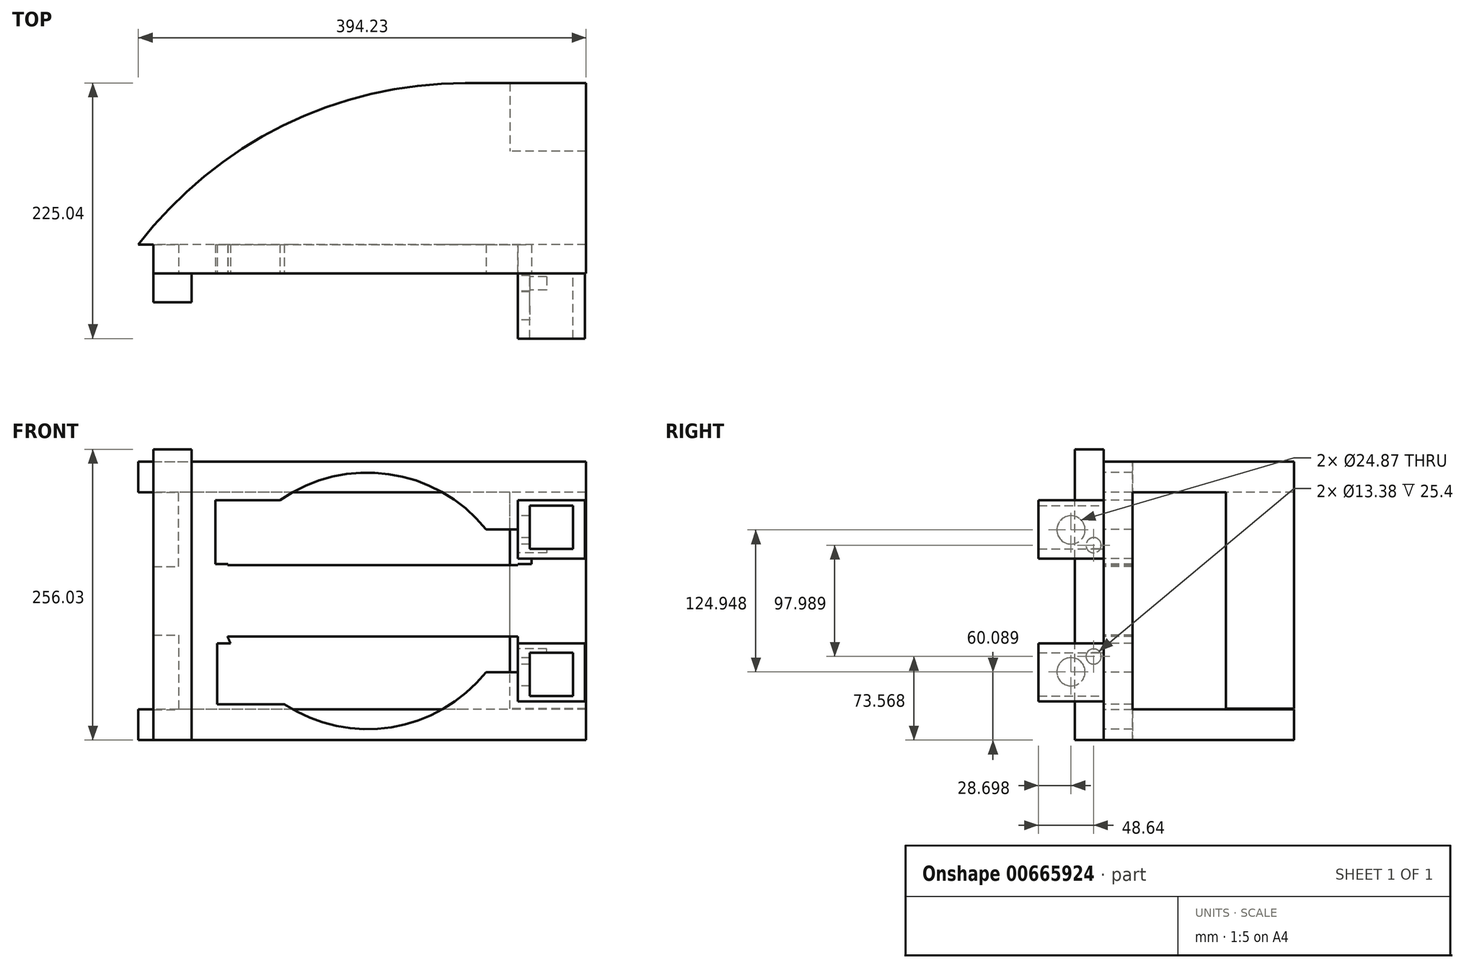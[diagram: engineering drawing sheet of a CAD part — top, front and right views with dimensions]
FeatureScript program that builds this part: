
annotation { "Feature Type Name" : "Feature", "Feature Type Description" : "" }
export const myFeature = defineFeature(function(context is Context, id is Id, definition is map)
    precondition{}
    {
        {
            var Q0;
            Q0=qCreatedBy(makeId("Front.planeOp"),FACE);
            var sketch = newSketch(context, id + "F0", { "sketchPlane" : qUnion([Q0])});
            skLineSegment(sketch, "E0.bottom", {"start": v(-19.97, 4.14) * mm, "end": v(18.13, 4.14) * mm});
            skLineSegment(sketch, "E0.top", {"start": v(-19.97, -33.96) * mm, "end": v(18.13, -33.96) * mm});
            skLineSegment(sketch, "E0.left", {"start": v(-19.97, 4.14) * mm, "end": v(-19.97, -33.96) * mm});
            skLineSegment(sketch, "E0.right", {"start": v(18.13, 4.14) * mm, "end": v(18.13, -33.96) * mm});
            skLineSegment(sketch, "E1.bottom", {"start": v(-30.53, 8.95) * mm, "end": v(28.42, 8.95) * mm});
            skLineSegment(sketch, "E1.top", {"start": v(-30.53, -42.29) * mm, "end": v(28.42, -42.29) * mm});
            skLineSegment(sketch, "E1.left", {"start": v(-30.53, 8.95) * mm, "end": v(-30.53, -42.29) * mm});
            skLineSegment(sketch, "E1.right", {"start": v(28.42, 8.95) * mm, "end": v(28.42, -42.29) * mm});
            skSolve(sketch);
        }
        {
            var Q0;
            Q0=makeQuery(id+"F0.imprint","IMPRINT",FACE,{"disambiguationData":[TD([[makeQuery(id+"F0.imprint","IMPRINT",EDGE,{"derivedFrom":sQuery(id+"F0.wireOp",EDGE,"E0.bottom")}),1.0]])]});
            extrude(context, id + "F1", {"entities" : qUnion([Q0]), "depth" : 57.4 * mm, "offsetDistance" : 25.4 * mm});
        }
        {
            var Q0;
            Q0=makeQuery(id+"F1.opExtrude","SWEPT_FACE",FACE,{"disambiguationData":[OSD([sQuery(id+"F0.wireOp",EDGE,"E1.left")])]});
            var sketch = newSketch(context, id + "F2", { "sketchPlane" : qUnion([Q0])});
            skCircle(sketch, "E2", {"center": v(28.7, -17.11) * mm, "radius": 12.44 * mm});
            skPoint(sketch, "E2.centerSnap0", {"position": v(28.7, 8.95) * mm});
            skSolve(sketch);
        }
        {
            var Q0;
            Q0 = qSketchRegion(id + "F2", true);
            extrude(context, id + "F3", {"entities" : qUnion([Q0]), "operationType" : NewBodyOperationType.REMOVE, "oppositeDirection" : true, "depth" : 25.4 * mm, "offsetDistance" : 25.4 * mm});
        }
        {
            var Q0;
            Q0=makeQuery(id+"F1.opExtrude","CAP_FACE",FACE,{"disambiguationData":[OSD([sQuery(id+"F0.wireOp",EDGE,"E0.bottom"),sQuery(id+"F0.wireOp",EDGE,"E0.top"),sQuery(id+"F0.wireOp",EDGE,"E0.left"),sQuery(id+"F0.wireOp",EDGE,"E0.right"),sQuery(id+"F0.wireOp",EDGE,"E1.bottom"),sQuery(id+"F0.wireOp",EDGE,"E1.top"),sQuery(id+"F0.wireOp",EDGE,"E1.left"),sQuery(id+"F0.wireOp",EDGE,"E1.right")])],"isStart":true});
            var sketch = newSketch(context, id + "F4", { "sketchPlane" : qUnion([Q0])});
            skLineSegment(sketch, "E3.bottom", {"start": v(74.53, 42.97) * mm, "end": v(-29.55, 42.97) * mm});
            skLineSegment(sketch, "E3.top", {"start": v(74.53, -79.59) * mm, "end": v(-29.55, -79.59) * mm});
            skLineSegment(sketch, "E3.left", {"start": v(74.53, 42.97) * mm, "end": v(74.53, -79.59) * mm});
            skLineSegment(sketch, "E3.right", {"start": v(-29.55, 42.97) * mm, "end": v(-29.55, -79.59) * mm});
            skSolve(sketch);
        }
        {
            var Q0;
            Q0 = qSketchRegion(id + "F4", true);
            extrude(context, id + "F5", {"entities" : qUnion([Q0]), "operationType" : NewBodyOperationType.ADD, "depth" : 25.4 * mm, "offsetDistance" : 25.4 * mm});
        }
        {
            var Q0;
            Q0=makeQuery(id+"F5.opExtrude","SWEPT_FACE",FACE,{"disambiguationData":[OSD([sQuery(id+"F4.wireOp",EDGE,"E3.left")])]});
            extrude(context, id + "F6", {"entities" : qUnion([Q0]), "operationType" : NewBodyOperationType.ADD, "depth" : 25.4 * mm, "offsetDistance" : 25.4 * mm});
        }
        {
            var Q0;
            Q0=makeQuery(id+"F1.opExtrude","SWEPT_FACE",FACE,{"disambiguationData":[OSD([sQuery(id+"F0.wireOp",EDGE,"E1.left")])]});
            var sketch = newSketch(context, id + "F7", { "sketchPlane" : qUnion([Q0])});
            skCircle(sketch, "E4", {"center": v(8.76, -30.6) * mm, "radius": 6.7 * mm});
            skSolve(sketch);
        }
        {
            var Q0;
            Q0 = qSketchRegion(id + "F7", true);
            extrude(context, id + "F8", {"entities" : qUnion([Q0]), "operationType" : NewBodyOperationType.REMOVE, "oppositeDirection" : true, "depth" : 25.4 * mm, "offsetDistance" : 25.4 * mm});
        }
        {
            var Q0;
            {var subQ0=sQuery(id+"F4.wireOp",EDGE,"E3.left");Q0=makeQuery(id+"F6.boolean.opBoolean","MERGE",FACE,{"derivedFrom":[makeQuery(id+"F5.opExtrude","CAP_FACE",FACE,{"disambiguationData":[OSD([sQuery(id+"F4.wireOp",EDGE,"E3.bottom"),sQuery(id+"F4.wireOp",EDGE,"E3.top"),subQ0,sQuery(id+"F4.wireOp",EDGE,"E3.right")])],"isStart":false}),makeQuery(id+"F6.opExtrude","SWEPT_FACE",FACE,{"disambiguationData":[OSD([subQ0]),TDD([makeQuery(id+"F5.opExtrude","CAP_EDGE",EDGE,{"disambiguationData":[OSD([subQ0])],"isStart":false})])]})]});}
            var sketch = newSketch(context, id + "F9", { "sketchPlane" : qUnion([Q0])});
            skLineSegment(sketch, "E5.bottom", {"start": v(-29.55, 15.94) * mm, "end": v(364.68, 15.94) * mm});
            skLineSegment(sketch, "E5.top", {"start": v(-29.55, 42.97) * mm, "end": v(364.68, 42.97) * mm});
            skLineSegment(sketch, "E5.left", {"start": v(-29.55, 15.94) * mm, "end": v(-29.55, 42.97) * mm});
            skLineSegment(sketch, "E5.right", {"start": v(364.68, 15.94) * mm, "end": v(364.68, 42.97) * mm});
            skSolve(sketch);
        }
        {
            var Q0;
            {var subQ0=sQuery(id+"F9.wireOp",EDGE,"E5.left");Q0=makeQuery(id+"F9.imprint","IMPRINT",FACE,{"disambiguationData":[TD([[makeQuery(id+"F9.imprint","IMPRINT",EDGE,{"derivedFrom":subQ0}),1.0]])]});}
            var Q1;
            {var subQ0=sQuery(id+"F9.wireOp",EDGE,"E5.right");Q1=makeQuery(id+"F9.imprint","IMPRINT",FACE,{"disambiguationData":[TD([[makeQuery(id+"F9.imprint","IMPRINT",EDGE,{"derivedFrom":subQ0}),1.0]])]});}
            extrude(context, id + "F10", {"entities" : qUnion([Q0, Q1]), "operationType" : NewBodyOperationType.ADD, "depth" : 142.24 * mm, "offsetDistance" : 25.4 * mm});
        }
        {
            var Q0;
            Q0=makeQuery(id+"F10.opExtrude","CAP_EDGE",EDGE,{"disambiguationData":[OSD([sQuery(id+"F9.wireOp",EDGE,"E5.right")])],"isStart":false});
            fillet(context, id + "F11", {"entities" : qUnion([Q0]), "radius" : 362.4 * mm, "tangentPropagation" : true, "allowEdgeOverflow" : false});
        }
        {
            var Q0;
            Q0=makeQuery(id+"F6.opExtrude","CAP_FACE",FACE,{"disambiguationData":[OSD([sQuery(id+"F4.wireOp",EDGE,"E3.left")])],"isStart":false});
            extrude(context, id + "F12", {"entities" : qUnion([Q0]), "operationType" : NewBodyOperationType.ADD, "depth" : 251.46 * mm, "offsetDistance" : 25.4 * mm});
        }
        {
            var Q0;
            {var subQ0=sQuery(id+"F4.wireOp",EDGE,"E3.left");var subQ1=makeQuery(id+"F5.opExtrude","CAP_EDGE",EDGE,{"disambiguationData":[OSD([subQ0])],"isStart":true});var subQ2=sQuery(id+"F4.wireOp",EDGE,"E3.top");var subQ3=sQuery(id+"F4.wireOp",EDGE,"E3.bottom");var subQ4=sQuery(id+"F4.wireOp",EDGE,"E3.right");Q0=makeQuery(id+"F12.boolean.opBoolean","MERGE",FACE,{"derivedFrom":[makeQuery(id+"F6.boolean.opBoolean","MERGE",FACE,{"derivedFrom":[makeQuery(id+"F5.boolean.opBoolean","SPLIT",FACE,{"disambiguationData":[TD([makeQuery(id+"F1.opExtrude","SWEPT_FACE",FACE,{"disambiguationData":[OSD([sQuery(id+"F0.wireOp",EDGE,"E1.bottom")])]})])],"derivedFrom":makeQuery(id+"F5.opExtrude","CAP_FACE",FACE,{"disambiguationData":[OSD([subQ3,subQ2,subQ0,subQ4])],"isStart":true})}),makeQuery(id+"F6.opExtrude","SWEPT_FACE",FACE,{"disambiguationData":[OSD([subQ0]),TDD([subQ1])]})]}),makeQuery(id+"F12.opExtrude","SWEPT_FACE",FACE,{"disambiguationData":[OSD([subQ0]),TDD([makeQuery(id+"F6.opExtrude","CAP_EDGE",EDGE,{"disambiguationData":[OSD([subQ0]),TDD([subQ1])],"isStart":false})])]})]});}
            var sketch = newSketch(context, id + "F13", { "sketchPlane" : qUnion([Q0])});
            skLineSegment(sketch, "E6.bottom", {"start": v(-351.4, -49.47) * mm, "end": v(-329.12, -49.47) * mm});
            skLineSegment(sketch, "E6.top", {"start": v(-351.4, 16.14) * mm, "end": v(-329.12, 16.14) * mm});
            skLineSegment(sketch, "E6.left", {"start": v(-351.4, -49.47) * mm, "end": v(-351.4, 16.14) * mm});
            skLineSegment(sketch, "E6.right", {"start": v(-329.12, -49.47) * mm, "end": v(-329.12, 16.14) * mm});
            skLineSegment(sketch, "E7.bottom", {"start": v(-329.12, -79.59) * mm, "end": v(-295.3, -79.59) * mm});
            skLineSegment(sketch, "E7.top", {"start": v(-329.12, 42.97) * mm, "end": v(-295.3, 42.97) * mm});
            skLineSegment(sketch, "E7.left", {"start": v(-329.12, -79.59) * mm, "end": v(-329.12, 42.97) * mm});
            skLineSegment(sketch, "E7.right", {"start": v(-295.3, -79.59) * mm, "end": v(-295.3, 42.97) * mm});
            skLineSegment(sketch, "E8.bottom", {"start": v(-295.3, -79.59) * mm, "end": v(-30.53, -79.59) * mm});
            skLineSegment(sketch, "E8.top", {"start": v(-295.3, -16.67) * mm, "end": v(-30.53, -16.67) * mm});
            skLineSegment(sketch, "E8.left", {"start": v(-295.3, -79.59) * mm, "end": v(-295.3, -16.67) * mm});
            skLineSegment(sketch, "E8.right", {"start": v(-30.53, -79.59) * mm, "end": v(-30.53, -16.67) * mm});
            skArc(sketch, "E9", {"start": v(-30.53, -79.59) * mm, "mid": v(-162.92, 33.33) * mm, "end": v(-295.3, -79.59) * mm});
            skLineSegment(sketch, "E10.top", {"start": v(-295.3, -48.13) * mm, "end": v(-30.53, -48.13) * mm});
            skLineSegment(sketch, "E10.left", {"start": v(-295.3, -79.59) * mm, "end": v(-295.3, -48.13) * mm});
            skLineSegment(sketch, "E10.right", {"start": v(-30.53, -79.59) * mm, "end": v(-30.53, -48.13) * mm});
            skSolve(sketch);
        }
        {
            var Q0;
            {var subQ0=sQuery(id+"F13.wireOp",EDGE,"E6.bottom");Q0=makeQuery(id+"F13.imprint","IMPRINT",FACE,{"disambiguationData":[TD([[makeQuery(id+"F13.imprint","IMPRINT",EDGE,{"derivedFrom":subQ0}),1.0]])]});}
            var Q1;
            {var subQ0=sQuery(id+"F13.wireOp",EDGE,"E10.right");Q1=makeQuery(id+"F13.imprint","IMPRINT",FACE,{"disambiguationData":[TD([[makeQuery(id+"F13.imprint","IMPRINT",EDGE,{"derivedFrom":subQ0}),1.0]])]});}
            var Q2;
            {var subQ0=sQuery(id+"F13.wireOp",EDGE,"E10.left");Q2=makeQuery(id+"F13.imprint","IMPRINT",FACE,{"disambiguationData":[TD([[makeQuery(id+"F13.imprint","IMPRINT",EDGE,{"derivedFrom":subQ0}),-1.0]])]});}
            var Q3;
            {var subQ2=sQuery(id+"F13.wireOp",EDGE,"E8.top");var subQ6=sQuery(id+"F13.wireOp",EDGE,"E9");var subQ7=makeQuery(id+"F13.imprint","INTERSECT",VERTEX,{"disambiguationData":[OD(1.0)],"derivedFrom":[subQ2,subQ6]});Q3=makeQuery(id+"F13.imprint","IMPRINT",FACE,{"disambiguationData":[TD([[makeQuery(id+"F13.imprint","IMPRINT",EDGE,{"disambiguationData":[TD([[subQ7,1.0]])],"derivedFrom":subQ6}),-1.0]])]});}
            var Q4;
            {var subQ0=sQuery(id+"F13.wireOp",EDGE,"E9");var subQ1=sQuery(id+"F13.wireOp",EDGE,"E8.top");var subQ2=makeQuery(id+"F13.imprint","INTERSECT",VERTEX,{"disambiguationData":[OD(0.0)],"derivedFrom":[subQ1,subQ0]});Q4=makeQuery(id+"F13.imprint","IMPRINT",FACE,{"disambiguationData":[TD([[makeQuery(id+"F13.imprint","IMPRINT",EDGE,{"disambiguationData":[TD([[subQ2,-1.0]])],"derivedFrom":subQ1}),-1.0]])]});}
            var Q5;
            {var subQ0=sQuery(id+"F13.wireOp",EDGE,"E9");var subQ1=sQuery(id+"F13.wireOp",EDGE,"E8.top");var subQ2=makeQuery(id+"F13.imprint","INTERSECT",VERTEX,{"disambiguationData":[OD(0.0)],"derivedFrom":[subQ1,subQ0]});Q5=makeQuery(id+"F13.imprint","IMPRINT",FACE,{"disambiguationData":[TD([[makeQuery(id+"F13.imprint","IMPRINT",EDGE,{"disambiguationData":[TD([[subQ2,-1.0]])],"derivedFrom":subQ1}),1.0]])]});}
            extrude(context, id + "F14", {"entities" : qUnion([Q0, Q1, Q2, Q3, Q4, Q5]), "operationType" : NewBodyOperationType.REMOVE, "oppositeDirection" : true, "depth" : 25.4 * mm, "offsetDistance" : 25.4 * mm});
        }
        {
            var Q0;
            Q0=makeQuery(id+"F1.opExtrude","SWEPT_BODY",BODY,{"disambiguationData":[OSD([sQuery(id+"F0.wireOp",EDGE,"E0.bottom"),sQuery(id+"F0.wireOp",EDGE,"E0.top"),sQuery(id+"F0.wireOp",EDGE,"E0.left"),sQuery(id+"F0.wireOp",EDGE,"E0.right"),sQuery(id+"F0.wireOp",EDGE,"E1.bottom"),sQuery(id+"F0.wireOp",EDGE,"E1.top"),sQuery(id+"F0.wireOp",EDGE,"E1.left"),sQuery(id+"F0.wireOp",EDGE,"E1.right")])]});
            var Q1;
            {var subQ0=sQuery(id+"F4.wireOp",EDGE,"E3.left");var subQ1=sQuery(id+"F4.wireOp",EDGE,"E3.top");Q1=makeQuery(id+"F12.boolean.opBoolean","MERGE",FACE,{"derivedFrom":[makeQuery(id+"F6.boolean.opBoolean","MERGE",FACE,{"derivedFrom":[makeQuery(id+"F5.opExtrude","SWEPT_FACE",FACE,{"disambiguationData":[OSD([subQ1])]}),makeQuery(id+"F6.opExtrude","SWEPT_FACE",FACE,{"disambiguationData":[OSD([subQ1,subQ0])]})]}),makeQuery(id+"F12.opExtrude","SWEPT_FACE",FACE,{"disambiguationData":[OSD([subQ1,subQ0])]})]});}
            mirror(context, id + "F15", {"operationType" : NewBodyOperationType.ADD, "entities" : qUnion([Q0]), "mirrorPlane" : qUnion([Q1])});
        }
        {
            var Q0;
            {var subQ0=sQuery(id+"F4.wireOp",EDGE,"E3.left");var subQ1=makeQuery(id+"F5.opExtrude","CAP_EDGE",EDGE,{"disambiguationData":[OSD([subQ0])],"isStart":true});var subQ2=sQuery(id+"F4.wireOp",EDGE,"E3.top");var subQ3=sQuery(id+"F4.wireOp",EDGE,"E3.bottom");var subQ4=sQuery(id+"F4.wireOp",EDGE,"E3.right");var subQ5=makeQuery(id+"F12.boolean.opBoolean","MERGE",FACE,{"derivedFrom":[makeQuery(id+"F6.boolean.opBoolean","MERGE",FACE,{"derivedFrom":[makeQuery(id+"F5.boolean.opBoolean","SPLIT",FACE,{"disambiguationData":[TD([makeQuery(id+"F1.opExtrude","SWEPT_FACE",FACE,{"disambiguationData":[OSD([sQuery(id+"F0.wireOp",EDGE,"E1.bottom")])]})])],"derivedFrom":makeQuery(id+"F5.opExtrude","CAP_FACE",FACE,{"disambiguationData":[OSD([subQ3,subQ2,subQ0,subQ4])],"isStart":true})}),makeQuery(id+"F6.opExtrude","SWEPT_FACE",FACE,{"disambiguationData":[OSD([subQ0]),TDD([subQ1])]})]}),makeQuery(id+"F12.opExtrude","SWEPT_FACE",FACE,{"disambiguationData":[OSD([subQ0]),TDD([makeQuery(id+"F6.opExtrude","CAP_EDGE",EDGE,{"disambiguationData":[OSD([subQ0]),TDD([subQ1])],"isStart":false})])]})]});Q0=makeQuery(id+"F15.boolean.opBoolean","MERGE",FACE,{"derivedFrom":[subQ5,makeQuery(id+"F15.opPattern","COPY",FACE,{"derivedFrom":subQ5,"instanceName":"1"})]});}
            var sketch = newSketch(context, id + "F16", { "sketchPlane" : qUnion([Q0])});
            skLineSegment(sketch, "E11.bottom", {"start": v(-351.4, -202.15) * mm, "end": v(-317.84, -202.15) * mm});
            skLineSegment(sketch, "E11.top", {"start": v(-351.4, 53.88) * mm, "end": v(-317.84, 53.88) * mm});
            skLineSegment(sketch, "E11.left", {"start": v(-351.4, -202.15) * mm, "end": v(-351.4, 53.88) * mm});
            skLineSegment(sketch, "E11.right", {"start": v(-317.84, -202.15) * mm, "end": v(-317.84, 53.88) * mm});
            skSolve(sketch);
        }
        {
            var Q0;
            Q0 = qSketchRegion(id + "F16", true);
            extrude(context, id + "F17", {"entities" : qUnion([Q0]), "operationType" : NewBodyOperationType.ADD, "depth" : 25.4 * mm, "offsetDistance" : 25.4 * mm});
        }
        {
            var Q0;
            {var subQ0=sQuery(id+"F4.wireOp",EDGE,"E3.left");var subQ1=makeQuery(id+"F5.opExtrude","CAP_EDGE",EDGE,{"disambiguationData":[OSD([subQ0])],"isStart":true});var subQ2=sQuery(id+"F4.wireOp",EDGE,"E3.top");var subQ3=sQuery(id+"F4.wireOp",EDGE,"E3.bottom");var subQ4=sQuery(id+"F4.wireOp",EDGE,"E3.right");var subQ5=makeQuery(id+"F12.boolean.opBoolean","MERGE",FACE,{"derivedFrom":[makeQuery(id+"F6.boolean.opBoolean","MERGE",FACE,{"derivedFrom":[makeQuery(id+"F5.boolean.opBoolean","SPLIT",FACE,{"disambiguationData":[TD([makeQuery(id+"F1.opExtrude","SWEPT_FACE",FACE,{"disambiguationData":[OSD([sQuery(id+"F0.wireOp",EDGE,"E1.bottom")])]})])],"derivedFrom":makeQuery(id+"F5.opExtrude","CAP_FACE",FACE,{"disambiguationData":[OSD([subQ3,subQ2,subQ0,subQ4])],"isStart":true})}),makeQuery(id+"F6.opExtrude","SWEPT_FACE",FACE,{"disambiguationData":[OSD([subQ0]),TDD([subQ1])]})]}),makeQuery(id+"F12.opExtrude","SWEPT_FACE",FACE,{"disambiguationData":[OSD([subQ0]),TDD([makeQuery(id+"F6.opExtrude","CAP_EDGE",EDGE,{"disambiguationData":[OSD([subQ0]),TDD([subQ1])],"isStart":false})])]})]});Q0=makeQuery(id+"F15.boolean.opBoolean","MERGE",FACE,{"derivedFrom":[subQ5,makeQuery(id+"F15.opPattern","COPY",FACE,{"derivedFrom":subQ5,"instanceName":"1"})]});}
            var sketch = newSketch(context, id + "F18", { "sketchPlane" : qUnion([Q0])});
            skLineSegment(sketch, "E12.bottom", {"start": v(-295.25, -170.69) * mm, "end": v(-30.53, -170.69) * mm});
            skLineSegment(sketch, "E12.top", {"start": v(-295.25, -116.89) * mm, "end": v(-30.53, -116.89) * mm});
            skLineSegment(sketch, "E12.left", {"start": v(-295.25, -170.69) * mm, "end": v(-295.25, -116.89) * mm});
            skLineSegment(sketch, "E12.right", {"start": v(-30.53, -170.69) * mm, "end": v(-30.53, -116.89) * mm});
            skLineSegment(sketch, "E13.bottom", {"start": v(-296.97, -47.1) * mm, "end": v(-18.5, -47.1) * mm});
            skLineSegment(sketch, "E13.top", {"start": v(-296.97, 8.95) * mm, "end": v(-18.5, 8.95) * mm});
            skLineSegment(sketch, "E13.left", {"start": v(-296.97, -47.1) * mm, "end": v(-296.97, 8.95) * mm});
            skLineSegment(sketch, "E13.right", {"start": v(-18.5, -47.1) * mm, "end": v(-18.5, 8.95) * mm});
            skSolve(sketch);
        }
        {
            var Q0;
            {var subQ2=sQuery(id+"F18.wireOp",EDGE,"E12.bottom");Q0=makeQuery(id+"F18.imprint","IMPRINT",FACE,{"disambiguationData":[TD([[makeQuery(id+"F18.imprint","IMPRINT",EDGE,{"derivedFrom":subQ2}),1.0]])]});}
            var Q1;
            {var subQ1=sQuery(id+"F18.wireOp",EDGE,"E13.bottom");Q1=makeQuery(id+"F18.imprint","IMPRINT",FACE,{"disambiguationData":[TD([[makeQuery(id+"F18.imprint","IMPRINT",EDGE,{"derivedFrom":subQ1}),1.0]])]});}
            extrude(context, id + "F19", {"entities" : qUnion([Q0, Q1]), "operationType" : NewBodyOperationType.REMOVE, "oppositeDirection" : true, "depth" : 25.4 * mm, "offsetDistance" : 25.4 * mm});
        }
        {
            var Q0;
            Q0=makeQuery(id+"F10.opExtrude","SWEPT_FACE",FACE,{"disambiguationData":[OSD([sQuery(id+"F9.wireOp",EDGE,"E5.bottom")])]});
            var sketch = newSketch(context, id + "F20", { "sketchPlane" : qUnion([Q0])});
            skLineSegment(sketch, "E14.bottom", {"start": v(29.55, -167.64) * mm, "end": v(-37.42, -167.64) * mm});
            skLineSegment(sketch, "E14.top", {"start": v(29.55, -107.71) * mm, "end": v(-37.42, -107.71) * mm});
            skLineSegment(sketch, "E14.left", {"start": v(29.55, -167.64) * mm, "end": v(29.55, -107.71) * mm});
            skLineSegment(sketch, "E14.right", {"start": v(-37.42, -167.64) * mm, "end": v(-37.42, -107.71) * mm});
            skSolve(sketch);
        }
        {
            var Q0;
            Q0 = qSketchRegion(id + "F20", true);
            extrude(context, id + "F21", {"entities" : qUnion([Q0]), "operationType" : NewBodyOperationType.ADD, "depth" : 190.5 * mm, "offsetDistance" : 25.4 * mm});
        }
    });
